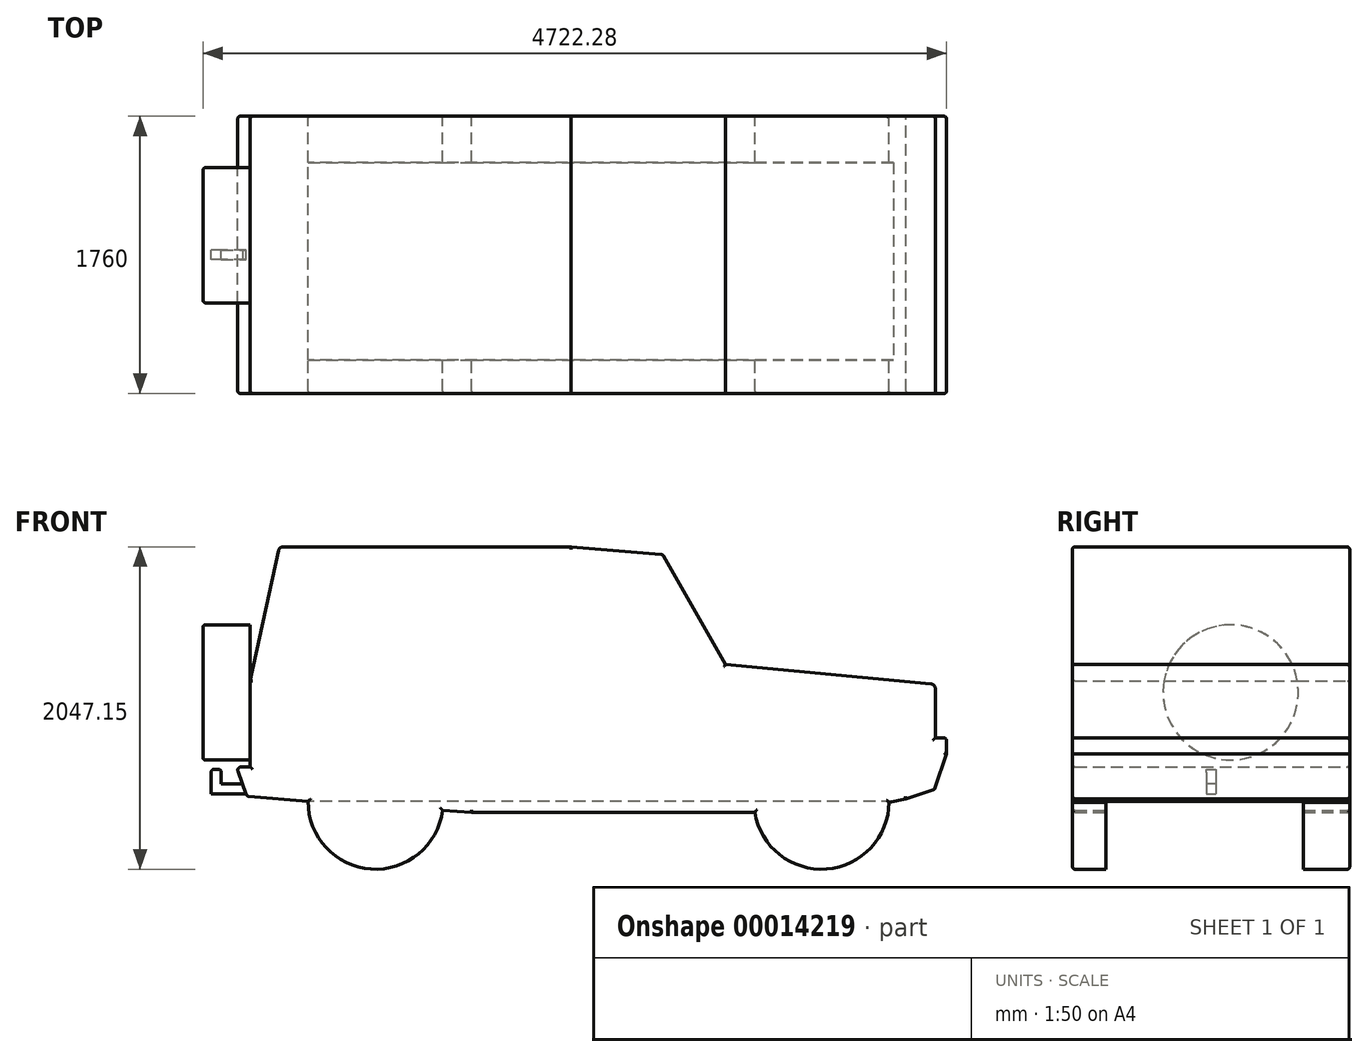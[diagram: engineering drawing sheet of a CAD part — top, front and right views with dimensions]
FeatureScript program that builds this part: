
annotation { "Feature Type Name" : "Feature", "Feature Type Description" : "" }
export const myFeature = defineFeature(function(context is Context, id is Id, definition is map)
    precondition{}
    {
        {
            var Q0;
            Q0=qCreatedBy(makeId("Front.planeOp"),FACE);
            var sketch = newSketch(context, id + "F0", { "sketchPlane" : qUnion([Q0])});
            skLineSegment(sketch, "E0.right", {"start": v(5794.5, 432.46) * mm, "end": v(5794.5, 515.63) * mm});
            skLineSegment(sketch, "E1", {"start": v(5695.98, 877.34) * mm, "end": v(4390.63, 1001.04) * mm});
            skLineSegment(sketch, "E2", {"start": v(4390.63, 1001.04) * mm, "end": v(3995.91, 1690.48) * mm});
            skLineSegment(sketch, "E3", {"start": v(3980.2, 1700.48) * mm, "end": v(3410.88, 1747.48) * mm});
            skLineSegment(sketch, "E4", {"start": v(3410.88, 1747.48) * mm, "end": v(1580.61, 1747.48) * mm});
            skLineSegment(sketch, "E5", {"start": v(1551.3, 1723.83) * mm, "end": v(1372.21, 896.91) * mm});
            skLineSegment(sketch, "E6", {"start": v(1372.21, 896.91) * mm, "end": v(1372.21, 349.37) * mm});
            skLineSegment(sketch, "E7", {"start": v(1372.21, 349.37) * mm, "end": v(1312.91, 349.37) * mm});
            skLineSegment(sketch, "E8", {"start": v(1294.04, 322.74) * mm, "end": v(1345.49, 176.32) * mm});
            skLineSegment(sketch, "E9", {"start": v(1362.7, 163.02) * mm, "end": v(1739.23, 131.64) * mm});
            skLineSegment(sketch, "E10", {"start": v(2593.64, 74) * mm, "end": v(2777.52, 62.11) * mm});
            skLineSegment(sketch, "E11", {"start": v(2777.52, 62.11) * mm, "end": v(4576.5, 62.11) * mm});
            skLineSegment(sketch, "E12", {"start": v(5429.19, 126) * mm, "end": v(5536.38, 147.99) * mm});
            skLineSegment(sketch, "E13", {"start": v(5536.38, 147.99) * mm, "end": v(5709.27, 203.93) * mm});
            skLineSegment(sketch, "E14", {"start": v(5722.08, 216.6) * mm, "end": v(5794.5, 432.46) * mm});
            skLineSegment(sketch, "E15", {"start": v(5723.15, 847.48) * mm, "end": v(5723.15, 535.63) * mm});
            skLineSegment(sketch, "E16", {"start": v(5723.15, 535.63) * mm, "end": v(5774.5, 535.63) * mm});
            skArc(sketch, "E17", {"start": v(4576.5, 62.11) * mm, "mid": v(5032.26, -298.47) * mm, "end": v(5429.19, 126) * mm});
            skArc(sketch, "E18", {"start": v(1739.23, 131.64) * mm, "mid": v(2139.35, -298.7) * mm, "end": v(2593.64, 74) * mm});
            skPoint(sketch, "E19.visualSharp", {"position": v(5723.15, 874.77) * mm});
            skArc(sketch, "E19.filletArc", {"start": v(5723.15, 847.48) * mm, "mid": v(5715.34, 867.66) * mm, "end": v(5695.98, 877.34) * mm});
            skPoint(sketch, "E20.visualSharp", {"position": v(3990.68, 1699.61) * mm});
            skArc(sketch, "E20.filletArc", {"start": v(3995.91, 1690.48) * mm, "mid": v(3989.3, 1697.42) * mm, "end": v(3980.2, 1700.48) * mm});
            skPoint(sketch, "E21.visualSharp", {"position": v(1556.41, 1747.48) * mm});
            skArc(sketch, "E21.filletArc", {"start": v(1580.61, 1747.48) * mm, "mid": v(1561.78, 1740.83) * mm, "end": v(1551.3, 1723.83) * mm});
            skPoint(sketch, "E22.visualSharp", {"position": v(1284.68, 349.37) * mm});
            skArc(sketch, "E22.filletArc", {"start": v(1312.91, 349.37) * mm, "mid": v(1296.6, 340.94) * mm, "end": v(1294.04, 322.74) * mm});
            skPoint(sketch, "E23.visualSharp", {"position": v(1349.78, 164.1) * mm});
            skArc(sketch, "E23.filletArc", {"start": v(1345.49, 176.32) * mm, "mid": v(1352.13, 167.12) * mm, "end": v(1362.7, 163.02) * mm});
            skPoint(sketch, "E24.visualSharp", {"position": v(5794.5, 535.63) * mm});
            skArc(sketch, "E24.filletArc", {"start": v(5794.5, 515.63) * mm, "mid": v(5788.64, 529.78) * mm, "end": v(5774.5, 535.63) * mm});
            skPoint(sketch, "E25.visualSharp", {"position": v(5718.87, 207.03) * mm});
            skArc(sketch, "E25.filletArc", {"start": v(5709.27, 203.93) * mm, "mid": v(5717.18, 208.74) * mm, "end": v(5722.08, 216.6) * mm});
            skSolve(sketch);
        }
        {
            var Q0;
            Q0=makeQuery(id+"F0.imprint","IMPRINT",FACE,{"disambiguationData":[TD([[makeQuery(id+"F0.imprint","IMPRINT",EDGE,{"derivedFrom":sQuery(id+"F0.wireOp",EDGE,"E0.right")}),1.0]])]});
            extrude(context, id + "F1", {"entities" : qUnion([Q0]), "endBound" : BoundingType.SYMMETRIC, "depth" : 1760 * mm});
        }
        {
            var Q0;
            Q0=makeQuery(id+"F1.opExtrude","SWEPT_FACE",FACE,{"disambiguationData":[OSD([sQuery(id+"F0.wireOp",EDGE,"E6")])]});
            var sketch = newSketch(context, id + "F2", { "sketchPlane" : qUnion([Q0])});
            skCircle(sketch, "E26", {"center": v(-124.53, 823.27) * mm, "radius": 429 * mm});
            skSolve(sketch);
        }
        {
            var Q0;
            {var subQ0=makeQuery(id+"F1.opExtrude","SWEPT_EDGE",EDGE,{"disambiguationData":[OSD([sQuery(id+"F0.wireOp",EDGE,"E5"),sQuery(id+"F0.wireOp",EDGE,"E6")])]});var subQ1=sQuery(id+"F2.wireOp",EDGE,"E26");var subQ3=makeQuery(id+"F2.imprint","INTERSECT",VERTEX,{"disambiguationData":[OD(0.0)],"derivedFrom":[subQ0,subQ1]});Q0=qUnion([makeQuery(id+"F2.imprint","IMPRINT",FACE,{"disambiguationData":[TD([[makeQuery(id+"F2.imprint","IMPRINT",EDGE,{"disambiguationData":[TD([[subQ3,1.0]])],"derivedFrom":subQ1}),1.0]])]}),makeQuery(id+"F2.imprint","IMPRINT",FACE,{"disambiguationData":[TD([[makeQuery(id+"F2.imprint","IMPRINT",EDGE,{"disambiguationData":[TD([[subQ3,-1.0]])],"derivedFrom":subQ1}),1.0]])]})]);}
            extrude(context, id + "F3", {"entities" : qUnion([Q0]), "operationType" : NewBodyOperationType.ADD, "depth" : 300 * mm});
        }
        {
            var Q0;
            Q0=qCreatedBy(makeId("Front.planeOp"),FACE);
            var sketch = newSketch(context, id + "F4", { "sketchPlane" : qUnion([Q0]), "asVersion" : FeatureScriptVersionNumber.V126_DCM_VERSION_64_3_1});
            skLineSegment(sketch, "E27.bottom", {"start": v(1167.98, 335.01) * mm, "end": v(1142.93, 335.01) * mm});
            skLineSegment(sketch, "E27.top", {"start": v(1187.98, 179.88) * mm, "end": v(1122.93, 179.88) * mm});
            skLineSegment(sketch, "E27.left", {"start": v(1187.98, 315.01) * mm, "end": v(1187.98, 242.44) * mm});
            skLineSegment(sketch, "E27.right", {"start": v(1122.93, 315.01) * mm, "end": v(1122.93, 179.88) * mm});
            skLineSegment(sketch, "E28.bottom", {"start": v(1187.98, 179.88) * mm, "end": v(1358.13, 179.88) * mm});
            skLineSegment(sketch, "E28.top", {"start": v(1187.98, 242.44) * mm, "end": v(1358.13, 242.44) * mm});
            skLineSegment(sketch, "E28.right", {"start": v(1358.13, 179.88) * mm, "end": v(1358.13, 242.44) * mm});
            skPoint(sketch, "E29.visualSharp", {"position": v(1187.98, 335.01) * mm});
            skArc(sketch, "E29.filletArc", {"start": v(1187.98, 315.01) * mm, "mid": v(1182.13, 329.16) * mm, "end": v(1167.98, 335.01) * mm});
            skPoint(sketch, "E30.visualSharp", {"position": v(1122.93, 335.01) * mm});
            skArc(sketch, "E30.filletArc", {"start": v(1142.93, 335.01) * mm, "mid": v(1128.79, 329.16) * mm, "end": v(1122.93, 315.01) * mm});
            skSolve(sketch);
        }
        {
            var Q0;
            Q0=qSketchRegion(id+"F4",true);
            extrude(context, id + "F5", {"entities" : qUnion([Q0]), "operationType" : NewBodyOperationType.ADD, "endBound" : BoundingType.SYMMETRIC, "depth" : 60 * mm});
        }
        {
            var Q0;
            Q0=qCreatedBy(makeId("Right.planeOp"),FACE);
            var sketch = newSketch(context, id + "F6", { "sketchPlane" : qUnion([Q0])});
            skLineSegment(sketch, "E31.bottom", {"start": v(587.34, -306.34) * mm, "end": v(-668.36, -306.34) * mm});
            skLineSegment(sketch, "E31.top", {"start": v(587.34, 131.64) * mm, "end": v(-668.36, 131.64) * mm});
            skLineSegment(sketch, "E31.left", {"start": v(587.34, -306.34) * mm, "end": v(587.34, 131.64) * mm});
            skLineSegment(sketch, "E31.right", {"start": v(-668.36, -306.34) * mm, "end": v(-668.36, 131.64) * mm});
            skSolve(sketch);
        }
        {
            var Q0;
            Q0=makeQuery(id+"F6.imprint","IMPRINT",FACE,{"disambiguationData":[TD([[makeQuery(id+"F6.imprint","IMPRINT",EDGE,{"derivedFrom":sQuery(id+"F6.wireOp",EDGE,"E31.bottom")}),-1.0]])]});
            extrude(context, id + "F7", {"entities" : qUnion([Q0]), "operationType" : NewBodyOperationType.REMOVE, "endBound" : BoundingType.THROUGH_ALL, "depth" : 25 * mm});
        }
        {
            var Q0;
            Q0=makeQuery(id+"F1.opExtrude","CAP_EDGE",EDGE,{"disambiguationData":[OSD([sQuery(id+"F0.wireOp",EDGE,"E1")])],"isStart":true});
            var Q1;
            Q1=makeQuery(id+"F1.opExtrude","CAP_EDGE",EDGE,{"disambiguationData":[OSD([sQuery(id+"F0.wireOp",EDGE,"E1")])],"isStart":false});
            var Q2;
            Q2=makeQuery(id+"F1.opExtrude","CAP_EDGE",EDGE,{"disambiguationData":[OSD([sQuery(id+"F0.wireOp",EDGE,"E2")])],"isStart":true});
            var Q3;
            Q3=makeQuery(id+"F1.opExtrude","CAP_EDGE",EDGE,{"disambiguationData":[OSD([sQuery(id+"F0.wireOp",EDGE,"E2")])],"isStart":false});
            var Q4;
            Q4=makeQuery(id+"F1.opExtrude","CAP_EDGE",EDGE,{"disambiguationData":[OSD([sQuery(id+"F0.wireOp",EDGE,"E3")])],"isStart":false});
            var Q5;
            Q5=makeQuery(id+"F1.opExtrude","CAP_EDGE",EDGE,{"disambiguationData":[OSD([sQuery(id+"F0.wireOp",EDGE,"E3")])],"isStart":true});
            var Q6;
            Q6=makeQuery(id+"F1.opExtrude","CAP_EDGE",EDGE,{"disambiguationData":[OSD([sQuery(id+"F0.wireOp",EDGE,"E4")])],"isStart":true});
            var Q7;
            Q7=makeQuery(id+"F1.opExtrude","CAP_EDGE",EDGE,{"disambiguationData":[OSD([sQuery(id+"F0.wireOp",EDGE,"E4")])],"isStart":false});
            var Q8;
            Q8=makeQuery(id+"F1.opExtrude","CAP_EDGE",EDGE,{"disambiguationData":[OSD([sQuery(id+"F0.wireOp",EDGE,"E6")])],"isStart":true});
            var Q9;
            Q9=makeQuery(id+"F1.opExtrude","CAP_EDGE",EDGE,{"disambiguationData":[OSD([sQuery(id+"F0.wireOp",EDGE,"E6")])],"isStart":false});
            var Q10;
            Q10=makeQuery(id+"F3.opExtrude","CAP_EDGE",EDGE,{"disambiguationData":[OSD([sQuery(id+"F2.wireOp",EDGE,"E26")])],"isStart":false});
            var Q11;
            Q11=makeQuery(id+"F1.opExtrude","CAP_FACE",FACE,{"disambiguationData":[OSD([sQuery(id+"F0.wireOp",EDGE,"E0.right"),sQuery(id+"F0.wireOp",EDGE,"E1"),sQuery(id+"F0.wireOp",EDGE,"E2"),sQuery(id+"F0.wireOp",EDGE,"E3"),sQuery(id+"F0.wireOp",EDGE,"E4"),sQuery(id+"F0.wireOp",EDGE,"E5"),sQuery(id+"F0.wireOp",EDGE,"E6"),sQuery(id+"F0.wireOp",EDGE,"E7"),sQuery(id+"F0.wireOp",EDGE,"E8"),sQuery(id+"F0.wireOp",EDGE,"E9"),sQuery(id+"F0.wireOp",EDGE,"E10"),sQuery(id+"F0.wireOp",EDGE,"E11"),sQuery(id+"F0.wireOp",EDGE,"E12"),sQuery(id+"F0.wireOp",EDGE,"E13"),sQuery(id+"F0.wireOp",EDGE,"E14"),sQuery(id+"F0.wireOp",EDGE,"E15"),sQuery(id+"F0.wireOp",EDGE,"E16"),sQuery(id+"F0.wireOp",EDGE,"E17"),sQuery(id+"F0.wireOp",EDGE,"E18"),sQuery(id+"F0.wireOp",EDGE,"E19.filletArc"),sQuery(id+"F0.wireOp",EDGE,"E20.filletArc"),sQuery(id+"F0.wireOp",EDGE,"E21.filletArc"),sQuery(id+"F0.wireOp",EDGE,"E22.filletArc"),sQuery(id+"F0.wireOp",EDGE,"E23.filletArc"),sQuery(id+"F0.wireOp",EDGE,"E24.filletArc"),sQuery(id+"F0.wireOp",EDGE,"E25.filletArc")])],"isStart":false});
            var Q12;
            Q12=makeQuery(id+"F1.opExtrude","CAP_FACE",FACE,{"disambiguationData":[OSD([sQuery(id+"F0.wireOp",EDGE,"E0.right"),sQuery(id+"F0.wireOp",EDGE,"E1"),sQuery(id+"F0.wireOp",EDGE,"E2"),sQuery(id+"F0.wireOp",EDGE,"E3"),sQuery(id+"F0.wireOp",EDGE,"E4"),sQuery(id+"F0.wireOp",EDGE,"E5"),sQuery(id+"F0.wireOp",EDGE,"E6"),sQuery(id+"F0.wireOp",EDGE,"E7"),sQuery(id+"F0.wireOp",EDGE,"E8"),sQuery(id+"F0.wireOp",EDGE,"E9"),sQuery(id+"F0.wireOp",EDGE,"E10"),sQuery(id+"F0.wireOp",EDGE,"E11"),sQuery(id+"F0.wireOp",EDGE,"E12"),sQuery(id+"F0.wireOp",EDGE,"E13"),sQuery(id+"F0.wireOp",EDGE,"E14"),sQuery(id+"F0.wireOp",EDGE,"E15"),sQuery(id+"F0.wireOp",EDGE,"E16"),sQuery(id+"F0.wireOp",EDGE,"E17"),sQuery(id+"F0.wireOp",EDGE,"E18"),sQuery(id+"F0.wireOp",EDGE,"E19.filletArc"),sQuery(id+"F0.wireOp",EDGE,"E20.filletArc"),sQuery(id+"F0.wireOp",EDGE,"E21.filletArc"),sQuery(id+"F0.wireOp",EDGE,"E22.filletArc"),sQuery(id+"F0.wireOp",EDGE,"E23.filletArc"),sQuery(id+"F0.wireOp",EDGE,"E24.filletArc"),sQuery(id+"F0.wireOp",EDGE,"E25.filletArc")])],"isStart":true});
            fillet(context, id + "F8", {"entities" : qUnion([Q0, Q1, Q2, Q3, Q4, Q5, Q6, Q7, Q8, Q9, Q10, Q11, Q12]), "radius" : 15 * mm, "tangentPropagation" : true, "allowEdgeOverflow" : false});
        }
    });
